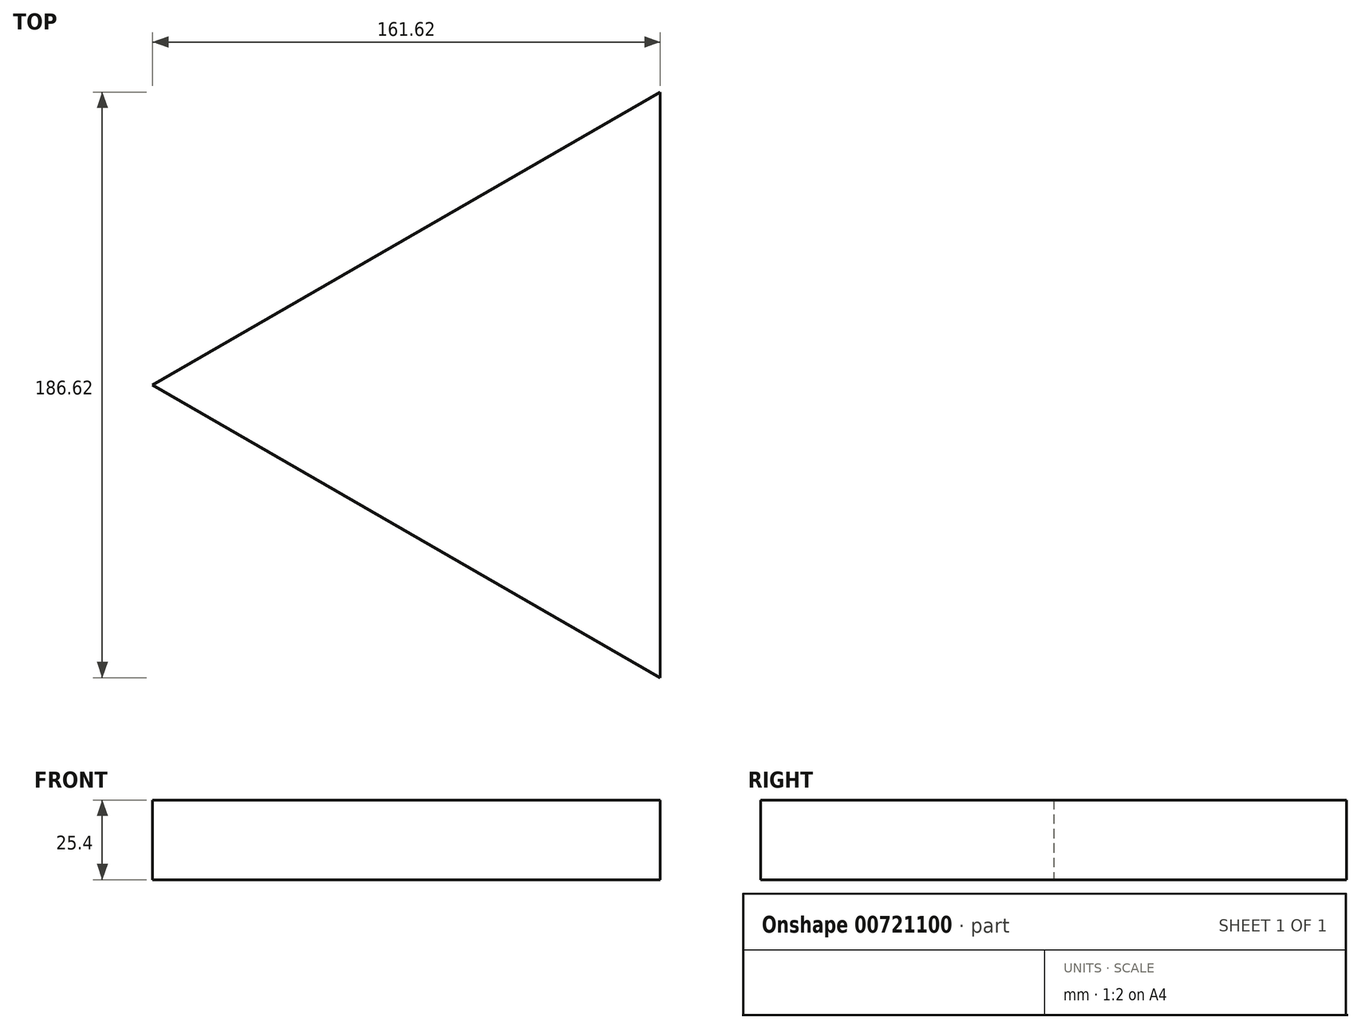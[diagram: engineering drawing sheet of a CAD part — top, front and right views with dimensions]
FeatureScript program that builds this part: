
annotation { "Feature Type Name" : "Feature", "Feature Type Description" : "" }
export const myFeature = defineFeature(function(context is Context, id is Id, definition is map)
    precondition{}
    {
        {
            var Q0;
            Q0=qCreatedBy(makeId("Top.planeOp"),FACE);
            var sketch = newSketch(context, id + "F0", { "sketchPlane" : qUnion([Q0])});
            skCircle(sketch, "E0.cCircle", {"center": v(-22.4, 7.45) * mm, "radius": 53.87 * mm, "construction": true});
            skLineSegment(sketch, "E0.0", {"start": v(31.47, 100.76) * mm, "end": v(31.47, -85.86) * mm});
            skLineSegment(sketch, "E0.1", {"start": v(31.47, -85.86) * mm, "end": v(-130.15, 7.45) * mm});
            skLineSegment(sketch, "E0.2", {"start": v(-130.15, 7.45) * mm, "end": v(31.47, 100.76) * mm});
            skPoint(sketch, "E0.0.midPoint", {"position": v(31.47, 7.45) * mm});
            skSolve(sketch);
        }
        {
            var Q0;
            Q0 = qSketchRegion(id + "F0", true);
            extrude(context, id + "F1", {"entities" : qUnion([Q0]), "depth" : 25.4 * mm, "offsetDistance" : 25.4 * mm});
        }
    });
